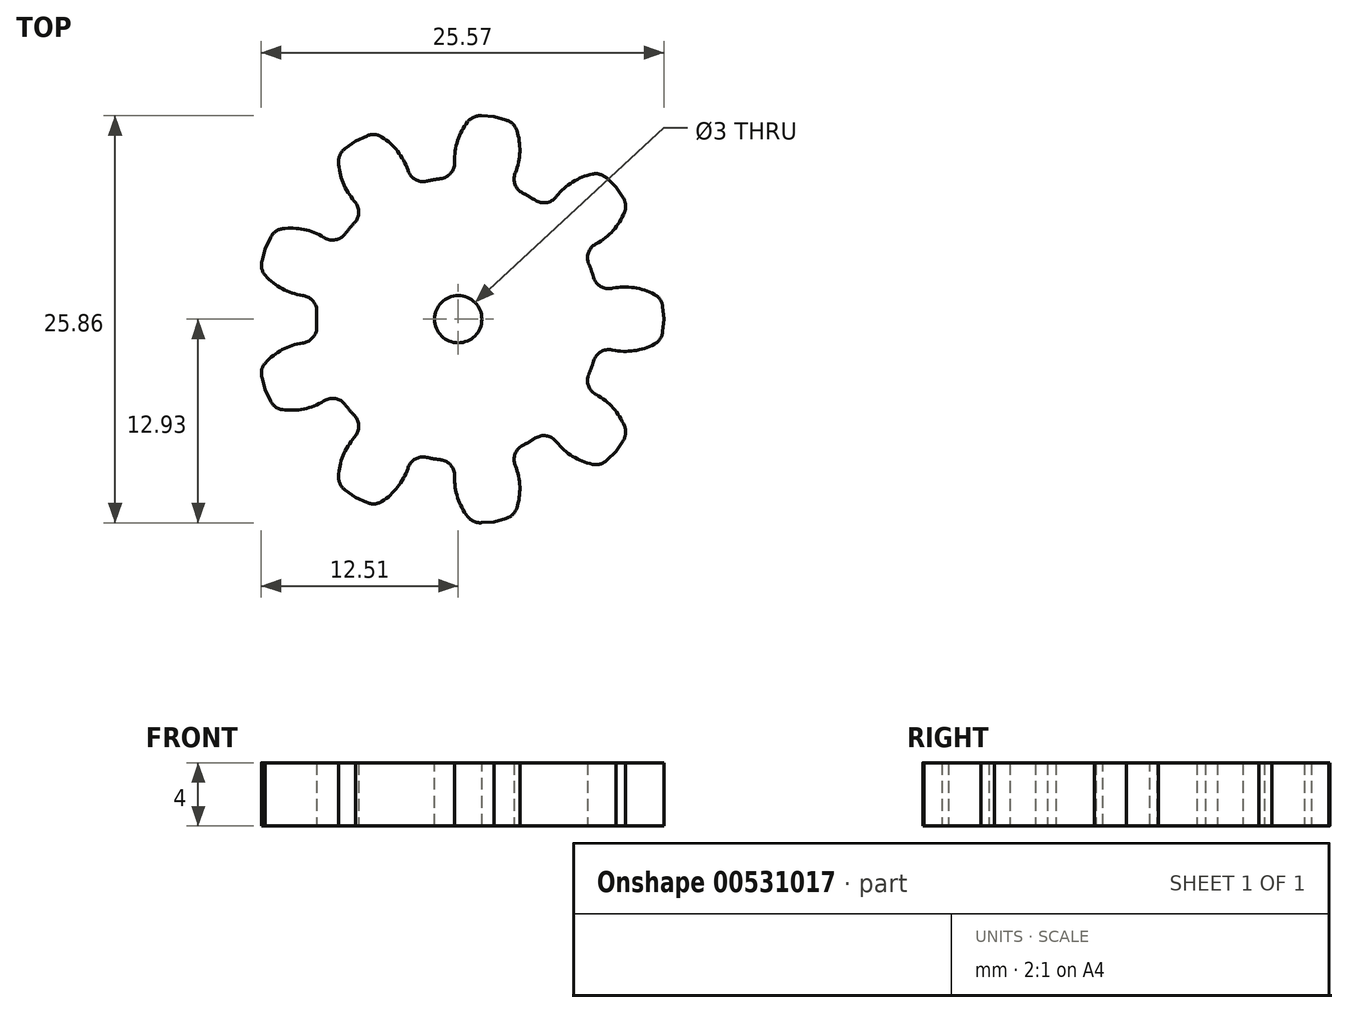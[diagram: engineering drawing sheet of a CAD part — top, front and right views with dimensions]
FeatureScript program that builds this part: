
annotation { "Feature Type Name" : "Feature", "Feature Type Description" : "" }
export const myFeature = defineFeature(function(context is Context, id is Id, definition is map)
    precondition{}
    {
        {
            var Q0;
            Q0=qCreatedBy(makeId("Top.planeOp"),FACE);
            var sketch = newSketch(context, id + "F0", { "sketchPlane" : qUnion([Q0])});
            skCircle(sketch, "E0", {"center": v(0, 0) * mm, "radius": 9 * mm, "construction": true});
            skLineSegment(sketch, "E1", {"start": v(0, 0) * mm, "end": v(11.56, 4.83) * mm, "construction": true});
            skLineSegment(sketch, "E2", {"start": v(0, 0) * mm, "end": v(13.06, 0) * mm, "construction": true});
            skLineSegment(sketch, "E3", {"start": v(0, 0) * mm, "end": v(8.3, 3.47) * mm});
            skLineSegment(sketch, "E4", {"start": v(0, 0) * mm, "end": v(9, 0) * mm});
            skLineSegment(sketch, "E5", {"start": v(0, 0) * mm, "end": v(9.8, 1.96) * mm, "construction": true});
            skLineSegment(sketch, "E6", {"start": v(0, 0) * mm, "end": v(12.94, 1.28) * mm, "construction": true});
            skArc(sketch, "E7", {"start": v(8.3, 3.47) * mm, "mid": v(8.46, 3.06) * mm, "end": v(8.6, 2.64) * mm});
            skLineSegment(sketch, "E8", {"start": v(9.76, 1.96) * mm, "end": v(9.8, 1.96) * mm});
            skLineSegment(sketch, "E9", {"start": v(12.98, 0.8) * mm, "end": v(13.06, 0) * mm});
            skLineSegment(sketch, "E10.MirrorCS", {"start": v(0, 0) * mm, "end": v(8.3, -3.47) * mm});
            skArc(sketch, "E11.MirrorCS", {"start": v(8.3, -3.47) * mm, "mid": v(8.46, -3.06) * mm, "end": v(8.6, -2.64) * mm});
            skLineSegment(sketch, "E12.MirrorCS", {"start": v(9.76, -1.96) * mm, "end": v(9.8, -1.96) * mm});
            skLineSegment(sketch, "E13.MirrorCS", {"start": v(12.98, -0.8) * mm, "end": v(13.06, 0) * mm});
            skPoint(sketch, "E14.visualSharp", {"position": v(8.82, 1.77) * mm});
            skArc(sketch, "E14.filletArc", {"start": v(8.6, 2.64) * mm, "mid": v(9.05, 2.08) * mm, "end": v(9.76, 1.96) * mm});
            skPoint(sketch, "E15.visualSharp", {"position": v(8.82, -1.77) * mm});
            skArc(sketch, "E15.filletArc", {"start": v(9.76, -1.96) * mm, "mid": v(9.05, -2.08) * mm, "end": v(8.6, -2.64) * mm});
            skPoint(sketch, "E16.visualSharp", {"position": v(12.94, -1.28) * mm});
            skArc(sketch, "E16.filletArc", {"start": v(12.46, -1.58) * mm, "mid": v(12.82, -1.26) * mm, "end": v(12.98, -0.8) * mm});
            skPoint(sketch, "E17.visualSharp", {"position": v(12.94, 1.28) * mm});
            skArc(sketch, "E17.filletArc", {"start": v(12.98, 0.8) * mm, "mid": v(12.82, 1.26) * mm, "end": v(12.46, 1.58) * mm});
            skArc(sketch, "E18", {"start": v(12.46, 1.58) * mm, "mid": v(11.16, 2) * mm, "end": v(9.8, 1.96) * mm});
            skArc(sketch, "E19", {"start": v(9.8, -1.96) * mm, "mid": v(11.16, -2) * mm, "end": v(12.46, -1.58) * mm});
            skSolve(sketch);
        }
        {
            var Q0;
            Q0=makeQuery(id+"F0.imprint","IMPRINT",FACE,{"disambiguationData":[TD([[makeQuery(id+"F0.imprint","IMPRINT",EDGE,{"derivedFrom":sQuery(id+"F0.wireOp",EDGE,"E3")}),-1.0]])]});
            extrude(context, id + "F1", {"entities" : qUnion([Q0]), "depth" : 4 * mm, "offsetDistance" : 25 * mm});
        }
        {
            var Q0;
            Q0=makeQuery(id+"F1.opExtrude","SWEPT_BODY",BODY,{"disambiguationData":[OSD([sQuery(id+"F0.wireOp",EDGE,"E3"),sQuery(id+"F0.wireOp",EDGE,"E7"),sQuery(id+"F0.wireOp",EDGE,"E8"),sQuery(id+"F0.wireOp",EDGE,"2mDmJFzi-9lNi-O13z-yd6C-LpkLtRZ1Arxh"),sQuery(id+"F0.wireOp",EDGE,"E9"),sQuery(id+"F0.wireOp",EDGE,"E10.MirrorCS"),sQuery(id+"F0.wireOp",EDGE,"E11.MirrorCS"),sQuery(id+"F0.wireOp",EDGE,"E12.MirrorCS"),sQuery(id+"F0.wireOp",EDGE,"b2a42f57-c3ba-47de-accf-343e7495cc910.MirrorCS"),sQuery(id+"F0.wireOp",EDGE,"E13.MirrorCS"),sQuery(id+"F0.wireOp",EDGE,"E14.filletArc"),sQuery(id+"F0.wireOp",EDGE,"E15.filletArc"),sQuery(id+"F0.wireOp",EDGE,"E16.filletArc"),sQuery(id+"F0.wireOp",EDGE,"E17.filletArc")])]});
            var Q1;
            Q1=makeQuery(id+"F1.opExtrude","SWEPT_EDGE",EDGE,{"disambiguationData":[OSD([sQuery(id+"F0.wireOp",EDGE,"E3"),sQuery(id+"F0.wireOp",EDGE,"E10.MirrorCS")])]});
            circularPattern(context, id + "F2", {"entities" : qUnion([Q0]), "axis" : qUnion([Q1]), "angle" : 360 * degree, "instanceCount" : 9, "equalSpace" : true, "computeTransformsWithoutBuiltin" : true});
        }
        {
            var Q0;
            Q0=makeQuery(id+"F2.opPattern","COPY",BODY,{"derivedFrom":makeQuery(id+"F1.opExtrude","SWEPT_BODY",BODY,{"disambiguationData":[OSD([sQuery(id+"F0.wireOp",EDGE,"E3"),sQuery(id+"F0.wireOp",EDGE,"E7"),sQuery(id+"F0.wireOp",EDGE,"E8"),sQuery(id+"F0.wireOp",EDGE,"2mDmJFzi-9lNi-O13z-yd6C-LpkLtRZ1Arxh"),sQuery(id+"F0.wireOp",EDGE,"E9"),sQuery(id+"F0.wireOp",EDGE,"E10.MirrorCS"),sQuery(id+"F0.wireOp",EDGE,"E11.MirrorCS"),sQuery(id+"F0.wireOp",EDGE,"E12.MirrorCS"),sQuery(id+"F0.wireOp",EDGE,"b2a42f57-c3ba-47de-accf-343e7495cc910.MirrorCS"),sQuery(id+"F0.wireOp",EDGE,"E13.MirrorCS"),sQuery(id+"F0.wireOp",EDGE,"E14.filletArc"),sQuery(id+"F0.wireOp",EDGE,"E15.filletArc"),sQuery(id+"F0.wireOp",EDGE,"E16.filletArc"),sQuery(id+"F0.wireOp",EDGE,"E17.filletArc")])]}),"instanceName":"7"});
            var Q1;
            Q1=makeQuery(id+"F2.opPattern","COPY",BODY,{"derivedFrom":makeQuery(id+"F1.opExtrude","SWEPT_BODY",BODY,{"disambiguationData":[OSD([sQuery(id+"F0.wireOp",EDGE,"E3"),sQuery(id+"F0.wireOp",EDGE,"E7"),sQuery(id+"F0.wireOp",EDGE,"E8"),sQuery(id+"F0.wireOp",EDGE,"2mDmJFzi-9lNi-O13z-yd6C-LpkLtRZ1Arxh"),sQuery(id+"F0.wireOp",EDGE,"E9"),sQuery(id+"F0.wireOp",EDGE,"E10.MirrorCS"),sQuery(id+"F0.wireOp",EDGE,"E11.MirrorCS"),sQuery(id+"F0.wireOp",EDGE,"E12.MirrorCS"),sQuery(id+"F0.wireOp",EDGE,"b2a42f57-c3ba-47de-accf-343e7495cc910.MirrorCS"),sQuery(id+"F0.wireOp",EDGE,"E13.MirrorCS"),sQuery(id+"F0.wireOp",EDGE,"E14.filletArc"),sQuery(id+"F0.wireOp",EDGE,"E15.filletArc"),sQuery(id+"F0.wireOp",EDGE,"E16.filletArc"),sQuery(id+"F0.wireOp",EDGE,"E17.filletArc")])]}),"instanceName":"6"});
            var Q2;
            Q2=makeQuery(id+"F2.opPattern","COPY",BODY,{"derivedFrom":makeQuery(id+"F1.opExtrude","SWEPT_BODY",BODY,{"disambiguationData":[OSD([sQuery(id+"F0.wireOp",EDGE,"E3"),sQuery(id+"F0.wireOp",EDGE,"E7"),sQuery(id+"F0.wireOp",EDGE,"E8"),sQuery(id+"F0.wireOp",EDGE,"2mDmJFzi-9lNi-O13z-yd6C-LpkLtRZ1Arxh"),sQuery(id+"F0.wireOp",EDGE,"E9"),sQuery(id+"F0.wireOp",EDGE,"E10.MirrorCS"),sQuery(id+"F0.wireOp",EDGE,"E11.MirrorCS"),sQuery(id+"F0.wireOp",EDGE,"E12.MirrorCS"),sQuery(id+"F0.wireOp",EDGE,"b2a42f57-c3ba-47de-accf-343e7495cc910.MirrorCS"),sQuery(id+"F0.wireOp",EDGE,"E13.MirrorCS"),sQuery(id+"F0.wireOp",EDGE,"E14.filletArc"),sQuery(id+"F0.wireOp",EDGE,"E15.filletArc"),sQuery(id+"F0.wireOp",EDGE,"E16.filletArc"),sQuery(id+"F0.wireOp",EDGE,"E17.filletArc")])]}),"instanceName":"4"});
            var Q3;
            Q3=makeQuery(id+"F2.opPattern","COPY",BODY,{"derivedFrom":makeQuery(id+"F1.opExtrude","SWEPT_BODY",BODY,{"disambiguationData":[OSD([sQuery(id+"F0.wireOp",EDGE,"E3"),sQuery(id+"F0.wireOp",EDGE,"E7"),sQuery(id+"F0.wireOp",EDGE,"E8"),sQuery(id+"F0.wireOp",EDGE,"2mDmJFzi-9lNi-O13z-yd6C-LpkLtRZ1Arxh"),sQuery(id+"F0.wireOp",EDGE,"E9"),sQuery(id+"F0.wireOp",EDGE,"E10.MirrorCS"),sQuery(id+"F0.wireOp",EDGE,"E11.MirrorCS"),sQuery(id+"F0.wireOp",EDGE,"E12.MirrorCS"),sQuery(id+"F0.wireOp",EDGE,"b2a42f57-c3ba-47de-accf-343e7495cc910.MirrorCS"),sQuery(id+"F0.wireOp",EDGE,"E13.MirrorCS"),sQuery(id+"F0.wireOp",EDGE,"E14.filletArc"),sQuery(id+"F0.wireOp",EDGE,"E15.filletArc"),sQuery(id+"F0.wireOp",EDGE,"E16.filletArc"),sQuery(id+"F0.wireOp",EDGE,"E17.filletArc")])]}),"instanceName":"5"});
            var Q4;
            Q4=makeQuery(id+"F1.opExtrude","SWEPT_BODY",BODY,{"disambiguationData":[OSD([sQuery(id+"F0.wireOp",EDGE,"E3"),sQuery(id+"F0.wireOp",EDGE,"E7"),sQuery(id+"F0.wireOp",EDGE,"E8"),sQuery(id+"F0.wireOp",EDGE,"2mDmJFzi-9lNi-O13z-yd6C-LpkLtRZ1Arxh"),sQuery(id+"F0.wireOp",EDGE,"E9"),sQuery(id+"F0.wireOp",EDGE,"E10.MirrorCS"),sQuery(id+"F0.wireOp",EDGE,"E11.MirrorCS"),sQuery(id+"F0.wireOp",EDGE,"E12.MirrorCS"),sQuery(id+"F0.wireOp",EDGE,"b2a42f57-c3ba-47de-accf-343e7495cc910.MirrorCS"),sQuery(id+"F0.wireOp",EDGE,"E13.MirrorCS"),sQuery(id+"F0.wireOp",EDGE,"E14.filletArc"),sQuery(id+"F0.wireOp",EDGE,"E15.filletArc"),sQuery(id+"F0.wireOp",EDGE,"E16.filletArc"),sQuery(id+"F0.wireOp",EDGE,"E17.filletArc")])]});
            var Q5;
            Q5=makeQuery(id+"F2.opPattern","COPY",BODY,{"derivedFrom":makeQuery(id+"F1.opExtrude","SWEPT_BODY",BODY,{"disambiguationData":[OSD([sQuery(id+"F0.wireOp",EDGE,"E3"),sQuery(id+"F0.wireOp",EDGE,"E7"),sQuery(id+"F0.wireOp",EDGE,"E8"),sQuery(id+"F0.wireOp",EDGE,"2mDmJFzi-9lNi-O13z-yd6C-LpkLtRZ1Arxh"),sQuery(id+"F0.wireOp",EDGE,"E9"),sQuery(id+"F0.wireOp",EDGE,"E10.MirrorCS"),sQuery(id+"F0.wireOp",EDGE,"E11.MirrorCS"),sQuery(id+"F0.wireOp",EDGE,"E12.MirrorCS"),sQuery(id+"F0.wireOp",EDGE,"b2a42f57-c3ba-47de-accf-343e7495cc910.MirrorCS"),sQuery(id+"F0.wireOp",EDGE,"E13.MirrorCS"),sQuery(id+"F0.wireOp",EDGE,"E14.filletArc"),sQuery(id+"F0.wireOp",EDGE,"E15.filletArc"),sQuery(id+"F0.wireOp",EDGE,"E16.filletArc"),sQuery(id+"F0.wireOp",EDGE,"E17.filletArc")])]}),"instanceName":"1"});
            var Q6;
            Q6=makeQuery(id+"F2.opPattern","COPY",BODY,{"derivedFrom":makeQuery(id+"F1.opExtrude","SWEPT_BODY",BODY,{"disambiguationData":[OSD([sQuery(id+"F0.wireOp",EDGE,"E3"),sQuery(id+"F0.wireOp",EDGE,"E7"),sQuery(id+"F0.wireOp",EDGE,"E8"),sQuery(id+"F0.wireOp",EDGE,"2mDmJFzi-9lNi-O13z-yd6C-LpkLtRZ1Arxh"),sQuery(id+"F0.wireOp",EDGE,"E9"),sQuery(id+"F0.wireOp",EDGE,"E10.MirrorCS"),sQuery(id+"F0.wireOp",EDGE,"E11.MirrorCS"),sQuery(id+"F0.wireOp",EDGE,"E12.MirrorCS"),sQuery(id+"F0.wireOp",EDGE,"b2a42f57-c3ba-47de-accf-343e7495cc910.MirrorCS"),sQuery(id+"F0.wireOp",EDGE,"E13.MirrorCS"),sQuery(id+"F0.wireOp",EDGE,"E14.filletArc"),sQuery(id+"F0.wireOp",EDGE,"E15.filletArc"),sQuery(id+"F0.wireOp",EDGE,"E16.filletArc"),sQuery(id+"F0.wireOp",EDGE,"E17.filletArc")])]}),"instanceName":"3"});
            var Q7;
            Q7=makeQuery(id+"F2.opPattern","COPY",BODY,{"derivedFrom":makeQuery(id+"F1.opExtrude","SWEPT_BODY",BODY,{"disambiguationData":[OSD([sQuery(id+"F0.wireOp",EDGE,"E3"),sQuery(id+"F0.wireOp",EDGE,"E7"),sQuery(id+"F0.wireOp",EDGE,"E8"),sQuery(id+"F0.wireOp",EDGE,"2mDmJFzi-9lNi-O13z-yd6C-LpkLtRZ1Arxh"),sQuery(id+"F0.wireOp",EDGE,"E9"),sQuery(id+"F0.wireOp",EDGE,"E10.MirrorCS"),sQuery(id+"F0.wireOp",EDGE,"E11.MirrorCS"),sQuery(id+"F0.wireOp",EDGE,"E12.MirrorCS"),sQuery(id+"F0.wireOp",EDGE,"b2a42f57-c3ba-47de-accf-343e7495cc910.MirrorCS"),sQuery(id+"F0.wireOp",EDGE,"E13.MirrorCS"),sQuery(id+"F0.wireOp",EDGE,"E14.filletArc"),sQuery(id+"F0.wireOp",EDGE,"E15.filletArc"),sQuery(id+"F0.wireOp",EDGE,"E16.filletArc"),sQuery(id+"F0.wireOp",EDGE,"E17.filletArc")])]}),"instanceName":"2"});
            var Q8;
            Q8=makeQuery(id+"F2.opPattern","COPY",BODY,{"derivedFrom":makeQuery(id+"F1.opExtrude","SWEPT_BODY",BODY,{"disambiguationData":[OSD([sQuery(id+"F0.wireOp",EDGE,"E3"),sQuery(id+"F0.wireOp",EDGE,"E7"),sQuery(id+"F0.wireOp",EDGE,"E8"),sQuery(id+"F0.wireOp",EDGE,"E9"),sQuery(id+"F0.wireOp",EDGE,"E10.MirrorCS"),sQuery(id+"F0.wireOp",EDGE,"E11.MirrorCS"),sQuery(id+"F0.wireOp",EDGE,"E12.MirrorCS"),sQuery(id+"F0.wireOp",EDGE,"E13.MirrorCS"),sQuery(id+"F0.wireOp",EDGE,"E14.filletArc"),sQuery(id+"F0.wireOp",EDGE,"E15.filletArc"),sQuery(id+"F0.wireOp",EDGE,"E16.filletArc"),sQuery(id+"F0.wireOp",EDGE,"E17.filletArc"),sQuery(id+"F0.wireOp",EDGE,"E18"),sQuery(id+"F0.wireOp",EDGE,"E19")])]}),"instanceName":"8"});
            booleanBodies(context, id + "F3", {"operationType" : BooleanOperationType.UNION, "tools" : qUnion([Q0, Q1, Q2, Q3, Q4, Q5, Q6, Q7, Q8])});
        }
        {
            var Q0;
            {var subQ0=makeQuery(id+"F1.opExtrude","CAP_FACE",FACE,{"disambiguationData":[OSD([sQuery(id+"F0.wireOp",EDGE,"E3"),sQuery(id+"F0.wireOp",EDGE,"E7"),sQuery(id+"F0.wireOp",EDGE,"E8"),sQuery(id+"F0.wireOp",EDGE,"E9"),sQuery(id+"F0.wireOp",EDGE,"E10.MirrorCS"),sQuery(id+"F0.wireOp",EDGE,"E11.MirrorCS"),sQuery(id+"F0.wireOp",EDGE,"E12.MirrorCS"),sQuery(id+"F0.wireOp",EDGE,"E13.MirrorCS"),sQuery(id+"F0.wireOp",EDGE,"E14.filletArc"),sQuery(id+"F0.wireOp",EDGE,"E15.filletArc"),sQuery(id+"F0.wireOp",EDGE,"E16.filletArc"),sQuery(id+"F0.wireOp",EDGE,"E17.filletArc"),sQuery(id+"F0.wireOp",EDGE,"E18"),sQuery(id+"F0.wireOp",EDGE,"E19")])],"isStart":false});Q0=makeQuery(id+"F3.opBoolean","MERGE",FACE,{"derivedFrom":[subQ0,makeQuery(id+"F2.opPattern","COPY",FACE,{"derivedFrom":subQ0,"instanceName":"1"}),makeQuery(id+"F2.opPattern","COPY",FACE,{"derivedFrom":subQ0,"instanceName":"2"}),makeQuery(id+"F2.opPattern","COPY",FACE,{"derivedFrom":subQ0,"instanceName":"3"}),makeQuery(id+"F2.opPattern","COPY",FACE,{"derivedFrom":subQ0,"instanceName":"4"}),makeQuery(id+"F2.opPattern","COPY",FACE,{"derivedFrom":subQ0,"instanceName":"5"}),makeQuery(id+"F2.opPattern","COPY",FACE,{"derivedFrom":subQ0,"instanceName":"6"}),makeQuery(id+"F2.opPattern","COPY",FACE,{"derivedFrom":subQ0,"instanceName":"7"}),makeQuery(id+"F2.opPattern","COPY",FACE,{"derivedFrom":subQ0,"instanceName":"8"})]});}
            var sketch = newSketch(context, id + "F4", { "sketchPlane" : qUnion([Q0])});
            skCircle(sketch, "E20", {"center": v(0, 0) * mm, "radius": 1.5 * mm});
            skSolve(sketch);
        }
        {
            var Q0;
            Q0=qSketchRegion(id+"F4",true);
            var Q1;
            {var subQ0=makeQuery(id+"F1.opExtrude","CAP_FACE",FACE,{"disambiguationData":[OSD([sQuery(id+"F0.wireOp",EDGE,"E3"),sQuery(id+"F0.wireOp",EDGE,"E7"),sQuery(id+"F0.wireOp",EDGE,"E8"),sQuery(id+"F0.wireOp",EDGE,"E9"),sQuery(id+"F0.wireOp",EDGE,"E10.MirrorCS"),sQuery(id+"F0.wireOp",EDGE,"E11.MirrorCS"),sQuery(id+"F0.wireOp",EDGE,"E12.MirrorCS"),sQuery(id+"F0.wireOp",EDGE,"E13.MirrorCS"),sQuery(id+"F0.wireOp",EDGE,"E14.filletArc"),sQuery(id+"F0.wireOp",EDGE,"E15.filletArc"),sQuery(id+"F0.wireOp",EDGE,"E16.filletArc"),sQuery(id+"F0.wireOp",EDGE,"E17.filletArc"),sQuery(id+"F0.wireOp",EDGE,"E18"),sQuery(id+"F0.wireOp",EDGE,"E19")])],"isStart":true});Q1=makeQuery(id+"F3.opBoolean","MERGE",FACE,{"derivedFrom":[subQ0,makeQuery(id+"F2.opPattern","COPY",FACE,{"derivedFrom":subQ0,"instanceName":"1"}),makeQuery(id+"F2.opPattern","COPY",FACE,{"derivedFrom":subQ0,"instanceName":"2"}),makeQuery(id+"F2.opPattern","COPY",FACE,{"derivedFrom":subQ0,"instanceName":"3"}),makeQuery(id+"F2.opPattern","COPY",FACE,{"derivedFrom":subQ0,"instanceName":"4"}),makeQuery(id+"F2.opPattern","COPY",FACE,{"derivedFrom":subQ0,"instanceName":"5"}),makeQuery(id+"F2.opPattern","COPY",FACE,{"derivedFrom":subQ0,"instanceName":"6"}),makeQuery(id+"F2.opPattern","COPY",FACE,{"derivedFrom":subQ0,"instanceName":"7"}),makeQuery(id+"F2.opPattern","COPY",FACE,{"derivedFrom":subQ0,"instanceName":"8"})]});}
            extrude(context, id + "F5", {"entities" : qUnion([Q0]), "operationType" : NewBodyOperationType.REMOVE, "endBound" : BoundingType.UP_TO_SURFACE, "oppositeDirection" : true, "depth" : 25 * mm, "endBoundEntityFace" : qUnion([Q1]), "offsetDistance" : 25 * mm});
        }
    });
